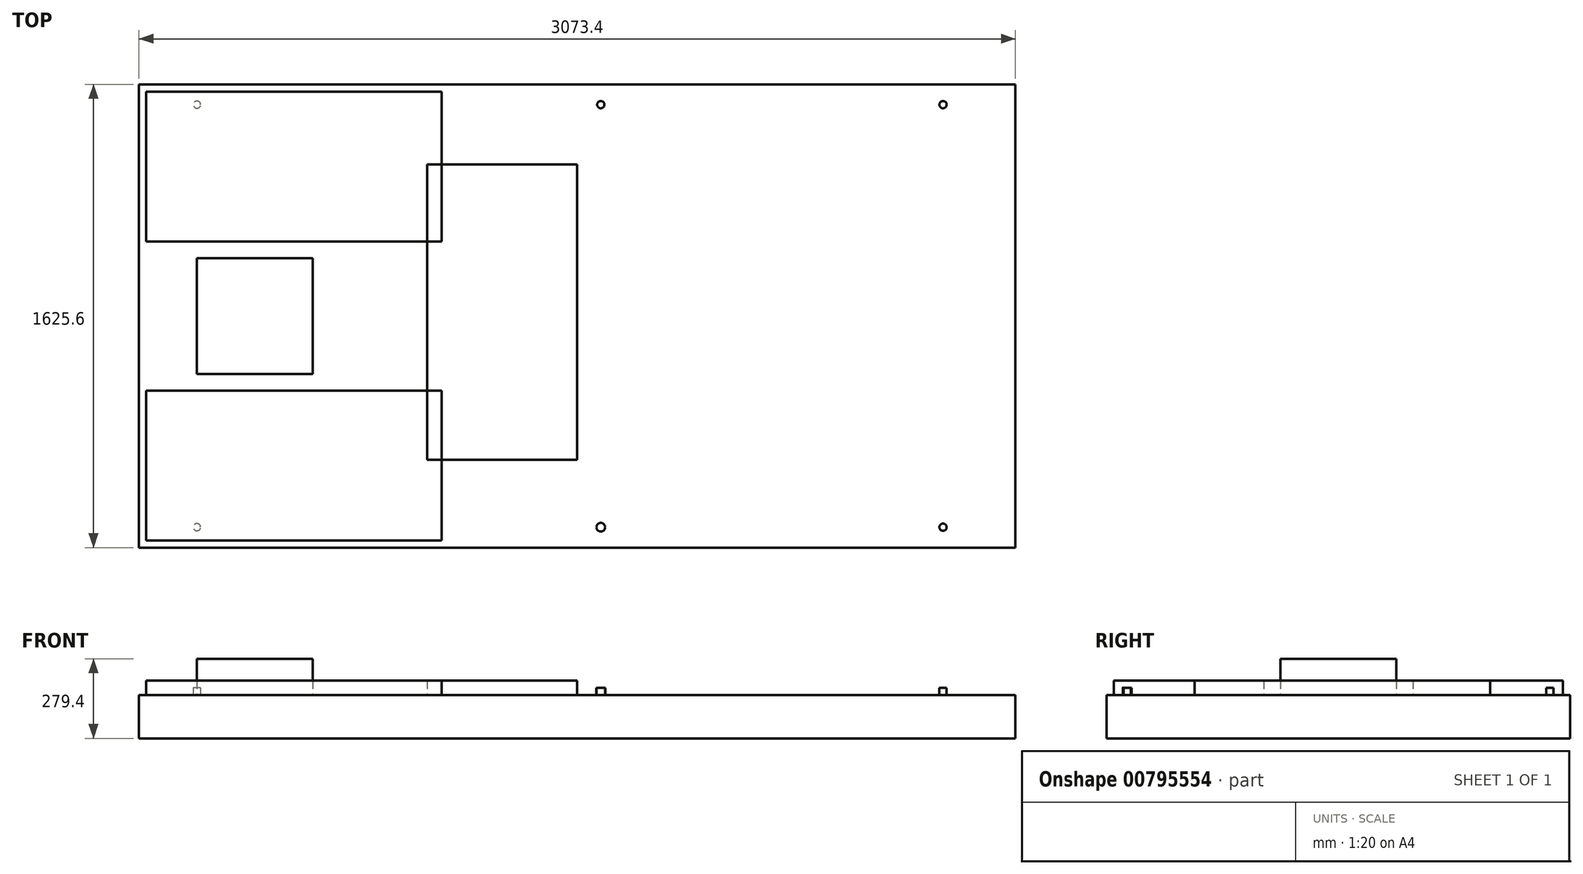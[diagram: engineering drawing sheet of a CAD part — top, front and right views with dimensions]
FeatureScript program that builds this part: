
annotation { "Feature Type Name" : "Feature", "Feature Type Description" : "" }
export const myFeature = defineFeature(function(context is Context, id is Id, definition is map)
    precondition{}
    {
        {
            var Q0;
            Q0=qCreatedBy(makeId("Top.planeOp"),FACE);
            var sketch = newSketch(context, id + "F0", { "sketchPlane" : qUnion([Q0])});
            skLineSegment(sketch, "E0.bottom", {"start": v(-1536.7, 812.8) * mm, "end": v(1536.7, 812.8) * mm});
            skLineSegment(sketch, "E0.top", {"start": v(-1536.7, -812.8) * mm, "end": v(1536.7, -812.8) * mm});
            skLineSegment(sketch, "E0.left", {"start": v(-1536.7, 812.8) * mm, "end": v(-1536.7, -812.8) * mm});
            skLineSegment(sketch, "E0.right", {"start": v(1536.7, 812.8) * mm, "end": v(1536.7, -812.8) * mm});
            skSolve(sketch);
        }
        {
            var Q0;
            Q0=qSketchRegion(id+"F0",true);
            extrude(context, id + "F1", {"entities" : qUnion([Q0]), "depth" : 152.4 * mm, "offsetDistance" : 25.4 * mm});
        }
        {
            var Q0;
            Q0=makeQuery(id+"F1.opExtrude","CAP_FACE",FACE,{"disambiguationData":[OSD([sQuery(id+"F0.wireOp",EDGE,"E0.bottom"),sQuery(id+"F0.wireOp",EDGE,"E0.top"),sQuery(id+"F0.wireOp",EDGE,"E0.left"),sQuery(id+"F0.wireOp",EDGE,"E0.right")])],"isStart":false});
            var sketch = newSketch(context, id + "F2", { "sketchPlane" : qUnion([Q0])});
            skLineSegment(sketch, "E1.bottom", {"start": v(-1333.5, 203.2) * mm, "end": v(-927.1, 203.2) * mm});
            skLineSegment(sketch, "E1.top", {"start": v(-1333.5, -203.2) * mm, "end": v(-927.1, -203.2) * mm});
            skLineSegment(sketch, "E1.left", {"start": v(-1333.5, 203.2) * mm, "end": v(-1333.5, -203.2) * mm});
            skLineSegment(sketch, "E1.right", {"start": v(-927.1, 203.2) * mm, "end": v(-927.1, -203.2) * mm});
            skSolve(sketch);
        }
        {
            var Q0;
            Q0=qSketchRegion(id+"F2",true);
            extrude(context, id + "F3", {"entities" : qUnion([Q0]), "operationType" : NewBodyOperationType.ADD, "depth" : 127 * mm, "offsetDistance" : 25.4 * mm});
        }
        {
            var Q0;
            Q0=makeQuery(id+"F1.opExtrude","CAP_FACE",FACE,{"disambiguationData":[OSD([sQuery(id+"F0.wireOp",EDGE,"E0.bottom"),sQuery(id+"F0.wireOp",EDGE,"E0.top"),sQuery(id+"F0.wireOp",EDGE,"E0.left"),sQuery(id+"F0.wireOp",EDGE,"E0.right")])],"isStart":false});
            var sketch = newSketch(context, id + "F4", { "sketchPlane" : qUnion([Q0])});
            skLineSegment(sketch, "E2.bottom", {"start": v(-1511.3, 787.4) * mm, "end": v(-474.98, 787.4) * mm});
            skLineSegment(sketch, "E2.top", {"start": v(-1511.3, 261.62) * mm, "end": v(-474.98, 261.62) * mm});
            skLineSegment(sketch, "E2.left", {"start": v(-1511.3, 787.4) * mm, "end": v(-1511.3, 261.62) * mm});
            skLineSegment(sketch, "E2.right", {"start": v(-474.98, 787.4) * mm, "end": v(-474.98, 261.62) * mm});
            skLineSegment(sketch, "E3", {"start": v(-1333.5, 0) * mm, "end": v(-285.57, 0) * mm});
            skLineSegment(sketch, "E4.MirrorCS", {"start": v(-1511.3, -261.62) * mm, "end": v(-474.98, -261.62) * mm});
            skLineSegment(sketch, "E5.MirrorCS", {"start": v(-474.98, -787.4) * mm, "end": v(-474.98, -261.62) * mm});
            skLineSegment(sketch, "E6.MirrorCS", {"start": v(-1511.3, -787.4) * mm, "end": v(-474.98, -787.4) * mm});
            skLineSegment(sketch, "E7.MirrorCS", {"start": v(-1511.3, -787.4) * mm, "end": v(-1511.3, -261.62) * mm});
            skSolve(sketch);
        }
        {
            var Q0;
            Q0=makeQuery(id+"F4.imprint","IMPRINT",FACE,{"disambiguationData":[TD([[makeQuery(id+"F4.imprint","IMPRINT",EDGE,{"derivedFrom":sQuery(id+"F4.wireOp",EDGE,"E4.MirrorCS")}),-1.0]])]});
            var Q1;
            Q1=makeQuery(id+"F4.imprint","IMPRINT",FACE,{"disambiguationData":[TD([[makeQuery(id+"F4.imprint","IMPRINT",EDGE,{"derivedFrom":sQuery(id+"F4.wireOp",EDGE,"E2.bottom")}),-1.0]])]});
            extrude(context, id + "F5", {"entities" : qUnion([Q0, Q1]), "depth" : 50.8 * mm, "offsetDistance" : 25.4 * mm});
        }
        {
            var Q0;
            Q0=makeQuery(id+"F1.opExtrude","CAP_FACE",FACE,{"disambiguationData":[OSD([sQuery(id+"F0.wireOp",EDGE,"E0.bottom"),sQuery(id+"F0.wireOp",EDGE,"E0.top"),sQuery(id+"F0.wireOp",EDGE,"E0.left"),sQuery(id+"F0.wireOp",EDGE,"E0.right")])],"isStart":false});
            var sketch = newSketch(context, id + "F6", { "sketchPlane" : qUnion([Q0])});
            skCircle(sketch, "E8", {"center": v(-1333.5, 741.36) * mm, "radius": 12.7 * mm});
            skCircle(sketch, "E9", {"center": v(-1333.5, -741.36) * mm, "radius": 12.7 * mm});
            skCircle(sketch, "E10", {"center": v(82.55, -741.36) * mm, "radius": 15.3 * mm});
            skCircle(sketch, "E11", {"center": v(1282.7, -741.36) * mm, "radius": 12.7 * mm});
            skCircle(sketch, "E12", {"center": v(1282.7, 741.36) * mm, "radius": 12.7 * mm});
            skCircle(sketch, "E13", {"center": v(82.55, 741.36) * mm, "radius": 12.7 * mm});
            skSolve(sketch);
        }
        {
            var Q0;
            Q0=qSketchRegion(id+"F6",true);
            extrude(context, id + "F7", {"entities" : qUnion([Q0]), "depth" : 25.4 * mm, "offsetDistance" : 25.4 * mm});
        }
        {
            var Q0;
            Q0=makeQuery(id+"F4.imprint","IMPRINT",FACE,{"disambiguationData":[TD([[makeQuery(id+"F4.imprint","IMPRINT",EDGE,{"derivedFrom":sQuery(id+"F4.wireOp",EDGE,"E2.bottom")}),1.0]])]});
            var sketch = newSketch(context, id + "F8", { "sketchPlane" : qUnion([Q0])});
            skLineSegment(sketch, "E14.bottom", {"start": v(-525.78, -504.93) * mm, "end": v(0, -504.93) * mm});
            skLineSegment(sketch, "E14.top", {"start": v(-525.78, 531.39) * mm, "end": v(0, 531.39) * mm});
            skLineSegment(sketch, "E14.left", {"start": v(-525.78, -504.93) * mm, "end": v(-525.78, 531.39) * mm});
            skLineSegment(sketch, "E14.right", {"start": v(0, -504.93) * mm, "end": v(0, 531.39) * mm});
            skSolve(sketch);
        }
        {
            var Q0;
            Q0 = qSketchRegion(id + "F8", true);
            extrude(context, id + "F9", {"entities" : qUnion([Q0]), "depth" : 50.8 * mm, "offsetDistance" : 25.4 * mm});
        }
    });
